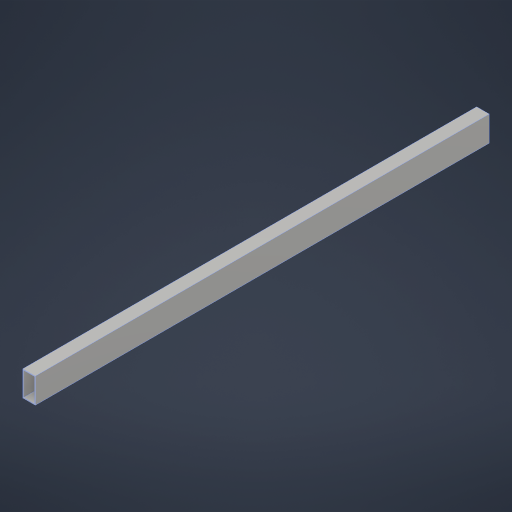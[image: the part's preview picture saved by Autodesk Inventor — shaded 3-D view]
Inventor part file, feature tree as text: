
AUTODESK INVENTOR PART (.ipt)
format: ipt  version: 2024.2 (Build 282272000, 272)  size: 174,592 bytes
history: native  units: in
note: dims shown in document units (in); Inventor stores cm internally (conversion verified against a paired STEP export)
features: extrude x1
ambient origin geometry x8: Origin, YZ Plane, XZ Plane, XY Plane, X Axis, Y Axis, Z Axis, Center Point
bodies: Solid1 (feature_tree)
feature tree (1):
  extrude  "Extrusion1"  TaperAngle=0.0deg  [1 undecoded]
note: 1 required parameter value undecoded (feature->parameter linkage not recoverable at this tier; creation-order binding heuristic only, values carry confidence <= 0.55)
